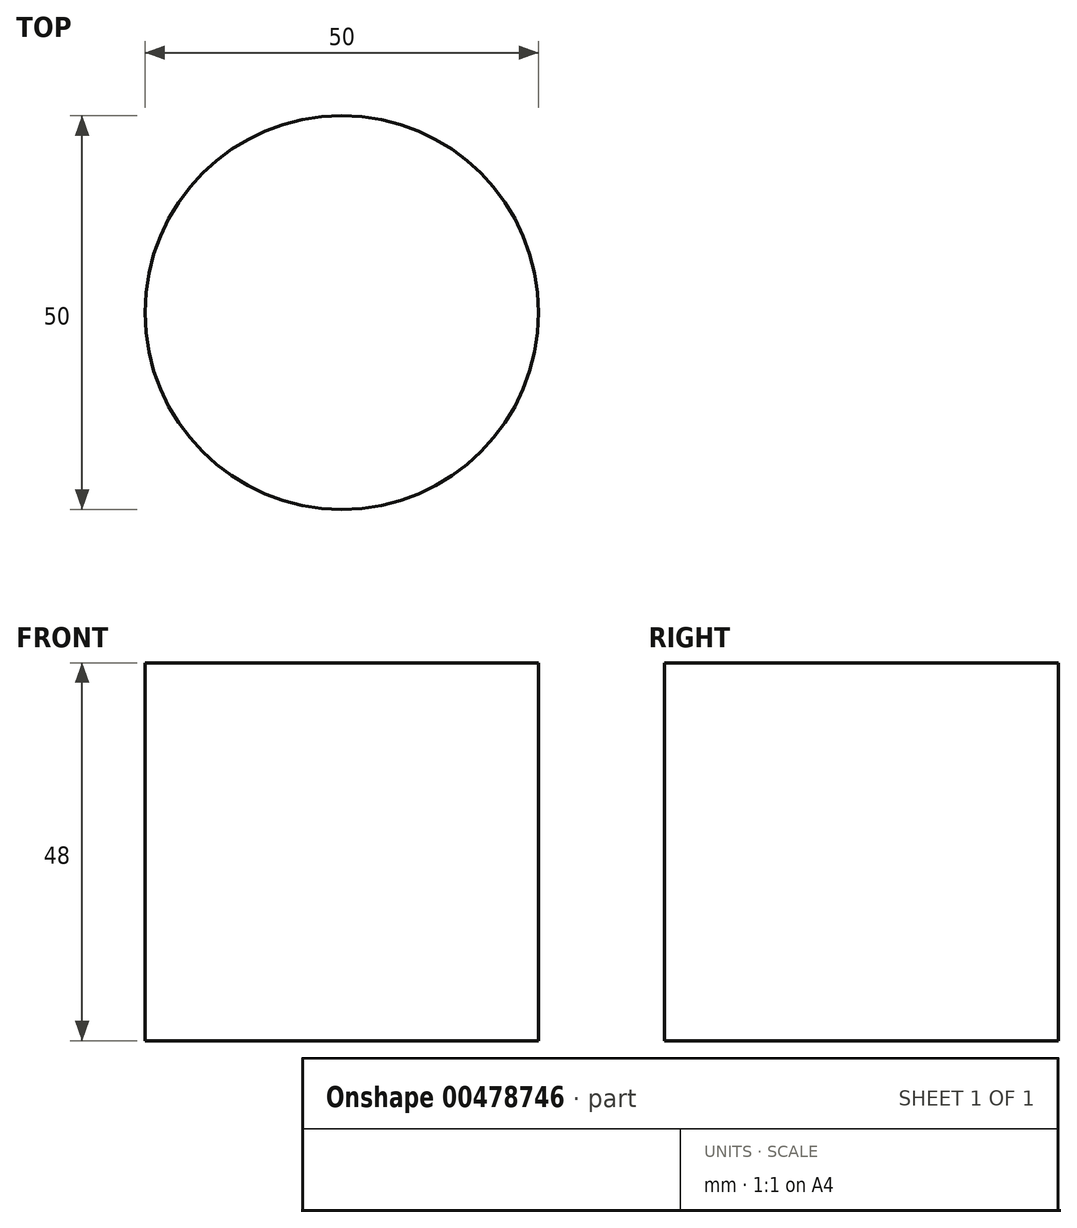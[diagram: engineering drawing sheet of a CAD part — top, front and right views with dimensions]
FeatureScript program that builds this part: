
annotation { "Feature Type Name" : "Feature", "Feature Type Description" : "" }
export const myFeature = defineFeature(function(context is Context, id is Id, definition is map)
    precondition{}
    {
        {
            var Q0;
            Q0=qCreatedBy(makeId("Top.planeOp"),FACE);
            var sketch = newSketch(context, id + "F0", { "sketchPlane" : qUnion([Q0])});
            skCircle(sketch, "E0", {"center": v(0, 0) * mm, "radius": 25 * mm});
            skSolve(sketch);
        }
        {
            var Q0;
            Q0 = qSketchRegion(id + "F0", true);
            extrude(context, id + "F1", {"entities" : qUnion([Q0]), "depth" : 48 * mm});
        }
    });
